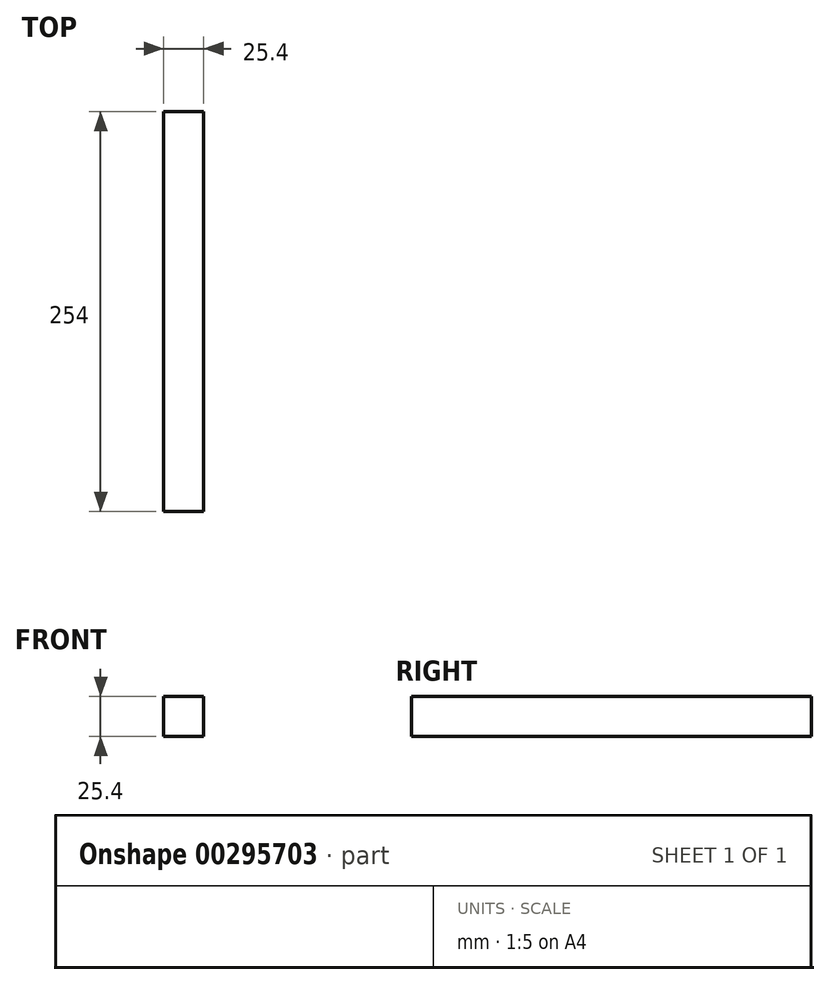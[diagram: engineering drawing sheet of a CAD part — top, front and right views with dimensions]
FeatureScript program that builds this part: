
annotation { "Feature Type Name" : "Feature", "Feature Type Description" : "" }
export const myFeature = defineFeature(function(context is Context, id is Id, definition is map)
    precondition{}
    {
        {
            var Q0;
            Q0=qCreatedBy(makeId("Right.planeOp"),FACE);
            var sketch = newSketch(context, id + "F0", { "sketchPlane" : qUnion([Q0])});
            skLineSegment(sketch, "E0.bottom", {"start": v(127, 12.7) * mm, "end": v(-127, 12.7) * mm});
            skLineSegment(sketch, "E0.top", {"start": v(127, -12.7) * mm, "end": v(-127, -12.7) * mm});
            skLineSegment(sketch, "E0.left", {"start": v(127, 12.7) * mm, "end": v(127, -12.7) * mm});
            skLineSegment(sketch, "E0.right", {"start": v(-127, 12.7) * mm, "end": v(-127, -12.7) * mm});
            skPoint(sketch, "E0.middle", {"position": v(0, 0) * mm});
            skSolve(sketch);
        }
        {
            var Q0;
            Q0 = qSketchRegion(id + "F0", true);
            extrude(context, id + "F1", {"entities" : qUnion([Q0]), "endBound" : BoundingType.SYMMETRIC, "depth" : 25.4 * mm});
        }
    });
